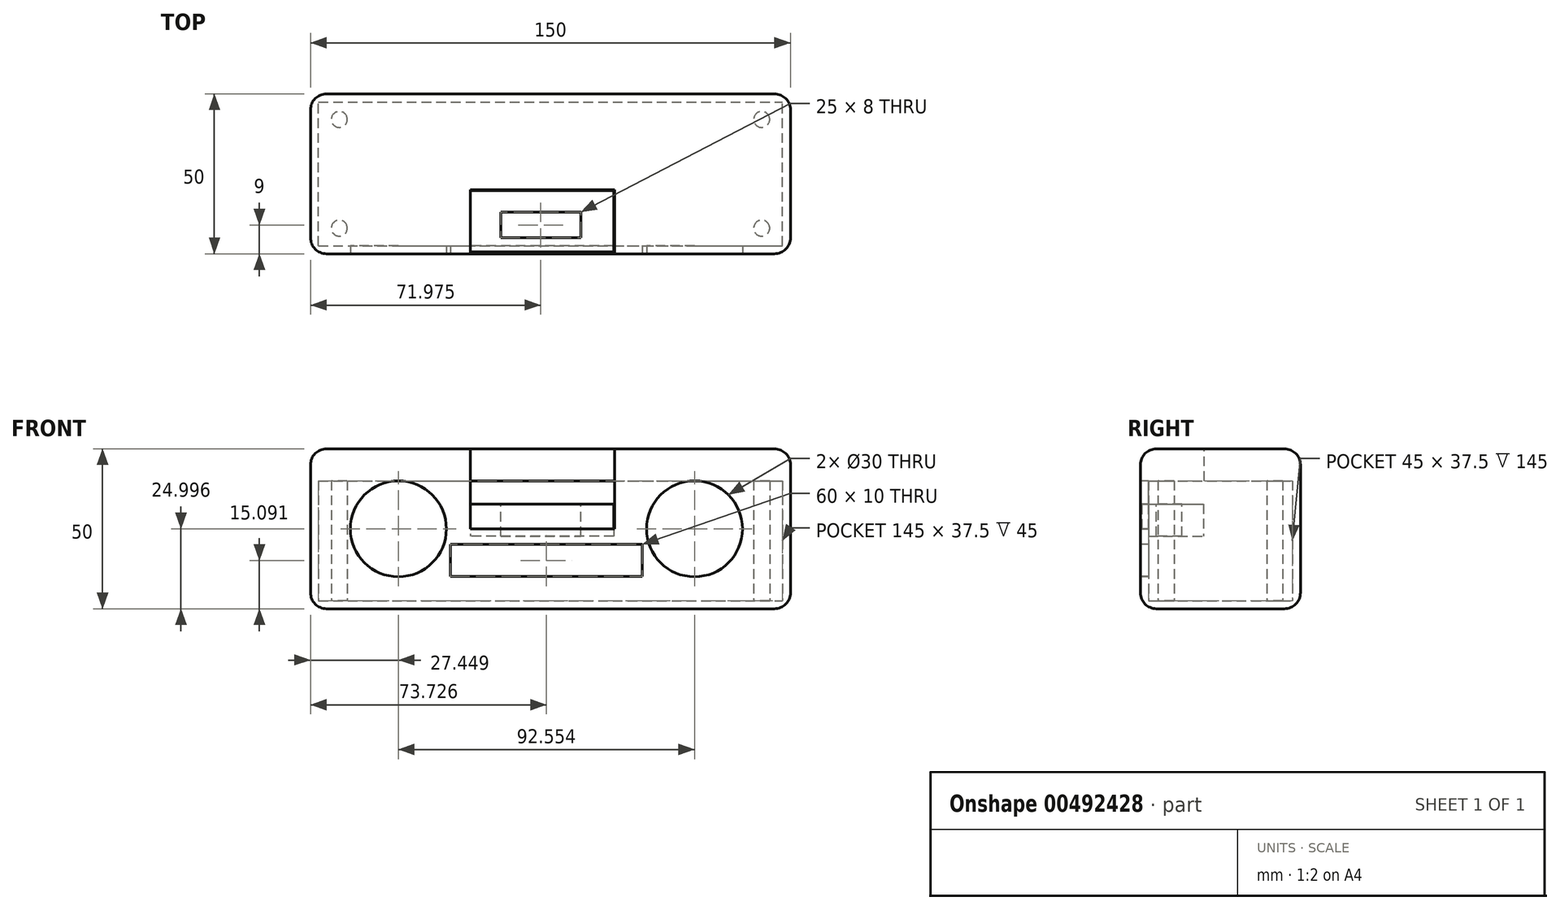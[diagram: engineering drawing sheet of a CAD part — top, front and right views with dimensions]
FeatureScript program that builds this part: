
annotation { "Feature Type Name" : "Feature", "Feature Type Description" : "" }
export const myFeature = defineFeature(function(context is Context, id is Id, definition is map)
    precondition{}
    {
        {
            var Q0;
            Q0=qCreatedBy(makeId("Front.planeOp"),FACE);
            var sketch = newSketch(context, id + "F0", { "sketchPlane" : qUnion([Q0])});
            skLineSegment(sketch, "E0.bottom", {"start": v(-76.49, 17.3) * mm, "end": v(73.51, 17.3) * mm});
            skLineSegment(sketch, "E0.top", {"start": v(-76.49, -22.7) * mm, "end": v(73.51, -22.7) * mm});
            skLineSegment(sketch, "E0.left", {"start": v(-76.49, 17.3) * mm, "end": v(-76.49, -22.7) * mm});
            skLineSegment(sketch, "E0.right", {"start": v(73.51, 17.3) * mm, "end": v(73.51, -22.7) * mm});
            skSolve(sketch);
        }
        {
            var Q0;
            Q0=makeQuery(id+"F0.imprint","IMPRINT",FACE,{"disambiguationData":[TD([[makeQuery(id+"F0.imprint","IMPRINT",EDGE,{"derivedFrom":sQuery(id+"F0.wireOp",EDGE,"E0.bottom")}),-1.0]])]});
            extrude(context, id + "F1", {"entities" : qUnion([Q0]), "depth" : 50 * mm});
        }
        {
            var Q0;
            Q0=makeQuery(id+"F1.opExtrude","SWEPT_FACE",FACE,{"disambiguationData":[OSD([sQuery(id+"F0.wireOp",EDGE,"E0.bottom")])]});
            shell(context, id + "F2", {"entities" : qUnion([Q0]), "thickness" : 2.5 * mm});
        }
        {
            var Q0;
            Q0=makeQuery(id+"F2.opShell","OFFSET_FACE",FACE,{"disambiguationData":[OSD([sQuery(id+"F0.wireOp",EDGE,"E0.top")])]});
            var sketch = newSketch(context, id + "F3", { "sketchPlane" : qUnion([Q0])});
            skCircle(sketch, "E1", {"center": v(-67.49, -8) * mm, "radius": 2.5 * mm});
            skSolve(sketch);
        }
        {
            var Q0;
            Q0=makeQuery(id+"F3.imprint","IMPRINT",FACE,{"disambiguationData":[TD([[makeQuery(id+"F3.imprint","IMPRINT",EDGE,{"derivedFrom":sQuery(id+"F3.wireOp",EDGE,"E1")}),-1.0]])]});
            var sketch = newSketch(context, id + "F4", { "sketchPlane" : qUnion([Q0])});
            skCircle(sketch, "E2", {"center": v(64.51, -8) * mm, "radius": 2.5 * mm});
            skSolve(sketch);
        }
        {
            var Q0;
            Q0=makeQuery(id+"F3.imprint","IMPRINT",FACE,{"disambiguationData":[TD([[makeQuery(id+"F3.imprint","IMPRINT",EDGE,{"derivedFrom":sQuery(id+"F3.wireOp",EDGE,"E1")}),-1.0]])]});
            var sketch = newSketch(context, id + "F5", { "sketchPlane" : qUnion([Q0])});
            skCircle(sketch, "E3", {"center": v(64.51, -42) * mm, "radius": 2.5 * mm});
            skSolve(sketch);
        }
        {
            var Q0;
            Q0=makeQuery(id+"F3.imprint","IMPRINT",FACE,{"disambiguationData":[TD([[makeQuery(id+"F3.imprint","IMPRINT",EDGE,{"derivedFrom":sQuery(id+"F3.wireOp",EDGE,"E1")}),-1.0]])]});
            var sketch = newSketch(context, id + "F6", { "sketchPlane" : qUnion([Q0])});
            skCircle(sketch, "E4", {"center": v(-67.49, -42) * mm, "radius": 2.5 * mm});
            skSolve(sketch);
        }
        {
            var Q0;
            Q0 = qSketchRegion(id + "F5", true);
            extrude(context, id + "F7", {"entities" : qUnion([Q0]), "operationType" : NewBodyOperationType.ADD, "depth" : 40 * mm});
        }
        {
            var Q0;
            Q0 = qSketchRegion(id + "F6", true);
            extrude(context, id + "F8", {"entities" : qUnion([Q0]), "operationType" : NewBodyOperationType.ADD, "depth" : 40 * mm});
        }
        {
            var Q0;
            Q0 = qSketchRegion(id + "F4", true);
            extrude(context, id + "F9", {"entities" : qUnion([Q0]), "operationType" : NewBodyOperationType.ADD, "depth" : 40 * mm});
        }
        {
            var Q0;
            Q0 = qSketchRegion(id + "F3", true);
            extrude(context, id + "F10", {"entities" : qUnion([Q0]), "operationType" : NewBodyOperationType.ADD, "depth" : 40 * mm});
        }
        {
            var Q0;
            Q0=makeQuery(id+"F1.opExtrude","SWEPT_FACE",FACE,{"disambiguationData":[OSD([sQuery(id+"F0.wireOp",EDGE,"E0.bottom")])]});
            var sketch = newSketch(context, id + "F11", { "sketchPlane" : qUnion([Q0])});
            skLineSegment(sketch, "E5.bottom", {"start": v(-76.49, 0) * mm, "end": v(73.51, 0) * mm});
            skLineSegment(sketch, "E5.top", {"start": v(-76.49, -50) * mm, "end": v(73.51, -50) * mm});
            skLineSegment(sketch, "E5.left", {"start": v(-76.49, 0) * mm, "end": v(-76.49, -50) * mm});
            skLineSegment(sketch, "E5.right", {"start": v(73.51, 0) * mm, "end": v(73.51, -50) * mm});
            skSolve(sketch);
        }
        {
            var Q0;
            Q0 = qSketchRegion(id + "F11", true);
            extrude(context, id + "F12", {"entities" : qUnion([Q0]), "operationType" : NewBodyOperationType.ADD, "depth" : 10 * mm});
        }
        {
            var Q0;
            Q0=makeQuery(id+"F12.opExtrude","CAP_FACE",FACE,{"disambiguationData":[OSD([sQuery(id+"F11.wireOp",EDGE,"E5.bottom"),sQuery(id+"F11.wireOp",EDGE,"E5.top"),sQuery(id+"F11.wireOp",EDGE,"E5.left"),sQuery(id+"F11.wireOp",EDGE,"E5.right")])],"isStart":false});
            var sketch = newSketch(context, id + "F13", { "sketchPlane" : qUnion([Q0])});
            skLineSegment(sketch, "E6.bottom", {"start": v(-26.49, -50) * mm, "end": v(18.51, -50) * mm});
            skLineSegment(sketch, "E6.top", {"start": v(-26.49, -30) * mm, "end": v(18.51, -30) * mm});
            skLineSegment(sketch, "E6.left", {"start": v(-26.49, -50) * mm, "end": v(-26.49, -30) * mm});
            skLineSegment(sketch, "E6.right", {"start": v(18.51, -50) * mm, "end": v(18.51, -30) * mm});
            skSolve(sketch);
        }
        {
            var Q0;
            Q0=makeQuery(id+"F13.imprint","IMPRINT",FACE,{"disambiguationData":[TD([[makeQuery(id+"F13.imprint","IMPRINT",EDGE,{"derivedFrom":sQuery(id+"F13.wireOp",EDGE,"E6.bottom")}),1.0]])]});
            extrude(context, id + "F14", {"entities" : qUnion([Q0]), "operationType" : NewBodyOperationType.REMOVE, "oppositeDirection" : true, "depth" : 25 * mm});
        }
        {
            var Q0;
            Q0=qCreatedBy(makeId("Top.planeOp"),FACE);
            var sketch = newSketch(context, id + "F15", { "sketchPlane" : qUnion([Q0])});
            skLineSegment(sketch, "E7.bottom", {"start": v(-26.54, -49.46) * mm, "end": v(18.27, -49.46) * mm});
            skLineSegment(sketch, "E7.top", {"start": v(-26.54, -30.26) * mm, "end": v(18.27, -30.26) * mm});
            skLineSegment(sketch, "E7.left", {"start": v(-26.54, -49.46) * mm, "end": v(-26.54, -30.26) * mm});
            skLineSegment(sketch, "E7.right", {"start": v(18.27, -49.46) * mm, "end": v(18.27, -30.26) * mm});
            skSolve(sketch);
        }
        {
            var Q0;
            Q0 = qSketchRegion(id + "F15", true);
            extrude(context, id + "F16", {"entities" : qUnion([Q0]), "operationType" : NewBodyOperationType.ADD, "depth" : 10 * mm});
        }
        {
            var Q0;
            Q0=makeQuery(id+"F16.opExtrude","CAP_FACE",FACE,{"disambiguationData":[OSD([sQuery(id+"F15.wireOp",EDGE,"E7.bottom"),sQuery(id+"F15.wireOp",EDGE,"E7.top"),sQuery(id+"F15.wireOp",EDGE,"E7.left"),sQuery(id+"F15.wireOp",EDGE,"E7.right")])],"isStart":false});
            var sketch = newSketch(context, id + "F17", { "sketchPlane" : qUnion([Q0])});
            skLineSegment(sketch, "E8.bottom", {"start": v(-17.02, -37) * mm, "end": v(7.98, -37) * mm});
            skLineSegment(sketch, "E8.top", {"start": v(-17.02, -45) * mm, "end": v(7.98, -45) * mm});
            skLineSegment(sketch, "E8.left", {"start": v(-17.02, -37) * mm, "end": v(-17.02, -45) * mm});
            skLineSegment(sketch, "E8.right", {"start": v(7.98, -37) * mm, "end": v(7.98, -45) * mm});
            skSolve(sketch);
        }
        {
            var Q0;
            Q0=makeQuery(id+"F17.imprint","IMPRINT",FACE,{"disambiguationData":[TD([[makeQuery(id+"F17.imprint","IMPRINT",EDGE,{"derivedFrom":sQuery(id+"F17.wireOp",EDGE,"E8.bottom")}),-1.0]])]});
            extrude(context, id + "F18", {"entities" : qUnion([Q0]), "operationType" : NewBodyOperationType.REMOVE, "oppositeDirection" : true, "depth" : 25 * mm});
        }
        {
            var Q0;
            Q0=makeQuery(id+"F12.boolean.opBoolean","MERGE",FACE,{"derivedFrom":[makeQuery(id+"F1.opExtrude","CAP_FACE",FACE,{"disambiguationData":[OSD([sQuery(id+"F0.wireOp",EDGE,"E0.bottom"),sQuery(id+"F0.wireOp",EDGE,"E0.top"),sQuery(id+"F0.wireOp",EDGE,"E0.left"),sQuery(id+"F0.wireOp",EDGE,"E0.right")])],"isStart":false}),makeQuery(id+"F12.opExtrude","SWEPT_FACE",FACE,{"disambiguationData":[OSD([sQuery(id+"F11.wireOp",EDGE,"E5.top")])]})]});
            var sketch = newSketch(context, id + "F19", { "sketchPlane" : qUnion([Q0])});
            skCircle(sketch, "E9", {"center": v(-49.04, 2.3) * mm, "radius": 15 * mm});
            skCircle(sketch, "E10", {"center": v(43.51, 2.3) * mm, "radius": 15 * mm});
            skSolve(sketch);
        }
        {
            var Q0;
            Q0=makeQuery(id+"F19.imprint","IMPRINT",FACE,{"disambiguationData":[TD([[makeQuery(id+"F19.imprint","IMPRINT",EDGE,{"derivedFrom":sQuery(id+"F19.wireOp",EDGE,"E9")}),1.0]])]});
            var Q1;
            Q1=makeQuery(id+"F19.imprint","IMPRINT",FACE,{"disambiguationData":[TD([[makeQuery(id+"F19.imprint","IMPRINT",EDGE,{"derivedFrom":sQuery(id+"F19.wireOp",EDGE,"E10")}),1.0]])]});
            extrude(context, id + "F20", {"entities" : qUnion([Q0, Q1]), "operationType" : NewBodyOperationType.REMOVE, "oppositeDirection" : true, "depth" : 5 * mm});
        }
        {
            var Q0;
            Q0=makeQuery(id+"F1.opExtrude","CAP_EDGE",EDGE,{"disambiguationData":[OSD([sQuery(id+"F0.wireOp",EDGE,"E0.top")])],"isStart":false});
            var Q1;
            Q1=makeQuery(id+"F1.opExtrude","SWEPT_EDGE",EDGE,{"disambiguationData":[OSD([sQuery(id+"F0.wireOp",EDGE,"E0.top"),sQuery(id+"F0.wireOp",EDGE,"E0.right")])]});
            var Q2;
            Q2=makeQuery(id+"F1.opExtrude","SWEPT_EDGE",EDGE,{"disambiguationData":[OSD([sQuery(id+"F0.wireOp",EDGE,"E0.top"),sQuery(id+"F0.wireOp",EDGE,"E0.left")])]});
            var Q3;
            Q3=makeQuery(id+"F1.opExtrude","CAP_EDGE",EDGE,{"disambiguationData":[OSD([sQuery(id+"F0.wireOp",EDGE,"E0.top")])],"isStart":true});
            var Q4;
            Q4=makeQuery(id+"F12.opExtrude","CAP_EDGE",EDGE,{"disambiguationData":[OSD([sQuery(id+"F11.wireOp",EDGE,"E5.bottom")])],"isStart":false});
            var Q5;
            {var subQ0=sQuery(id+"F11.wireOp",EDGE,"E5.top");var subQ1=sQuery(id+"F0.wireOp",EDGE,"E0.left");Q5=makeQuery(id+"F14.boolean.opBoolean","SPLIT",EDGE,{"disambiguationData":[TD([makeQuery(id+"F1.opExtrude","SWEPT_FACE",FACE,{"disambiguationData":[OSD([subQ1])]})])],"derivedFrom":makeQuery(id+"F12.opExtrude","CAP_EDGE",EDGE,{"disambiguationData":[OSD([subQ0])],"isStart":false})});}
            fillet(context, id + "F21", {"entities" : qUnion([Q0, Q1, Q2, Q3, Q4, Q5]), "radius" : 5 * mm, "tangentPropagation" : true, "allowEdgeOverflow" : false});
        }
        {
            var Q0;
            Q0=makeQuery(id+"F12.opExtrude","CAP_EDGE",EDGE,{"disambiguationData":[OSD([sQuery(id+"F11.wireOp",EDGE,"E5.right")])],"isStart":false});
            var Q1;
            Q1=makeQuery(id+"F12.opExtrude","CAP_EDGE",EDGE,{"disambiguationData":[OSD([sQuery(id+"F11.wireOp",EDGE,"E5.left")])],"isStart":false});
            var Q2;
            Q2=makeQuery(id+"F12.boolean.opBoolean","MERGE",EDGE,{"derivedFrom":[makeQuery(id+"F1.opExtrude","CAP_EDGE",EDGE,{"disambiguationData":[OSD([sQuery(id+"F0.wireOp",EDGE,"E0.right")])],"isStart":false}),makeQuery(id+"F12.opExtrude","SWEPT_EDGE",EDGE,{"disambiguationData":[OSD([sQuery(id+"F11.wireOp",EDGE,"E5.top"),sQuery(id+"F11.wireOp",EDGE,"E5.right")])]})]});
            fillet(context, id + "F22", {"entities" : qUnion([Q0, Q1, Q2]), "radius" : 5 * mm, "tangentPropagation" : true, "allowEdgeOverflow" : false});
        }
        {
            var Q0;
            {var subQ0=sQuery(id+"F11.wireOp",EDGE,"E5.top");var subQ1=sQuery(id+"F0.wireOp",EDGE,"E0.right");Q0=makeQuery(id+"F14.boolean.opBoolean","SPLIT",EDGE,{"disambiguationData":[TD([makeQuery(id+"F1.opExtrude","SWEPT_FACE",FACE,{"disambiguationData":[OSD([subQ1])]})])],"derivedFrom":makeQuery(id+"F12.opExtrude","CAP_EDGE",EDGE,{"disambiguationData":[OSD([subQ0])],"isStart":false})});}
            fillet(context, id + "F23", {"entities" : qUnion([Q0]), "radius" : 5 * mm, "tangentPropagation" : true, "allowEdgeOverflow" : false});
        }
        {
            var Q0;
            Q0=makeQuery(id+"F19.imprint","IMPRINT",FACE,{"disambiguationData":[TD([[makeQuery(id+"F19.imprint","IMPRINT",EDGE,{"derivedFrom":sQuery(id+"F19.wireOp",EDGE,"E9")}),-1.0]])]});
            var sketch = newSketch(context, id + "F24", { "sketchPlane" : qUnion([Q0])});
            skLineSegment(sketch, "E11.bottom", {"start": v(-32.76, -2.6) * mm, "end": v(27.24, -2.6) * mm});
            skLineSegment(sketch, "E11.top", {"start": v(-32.76, -12.6) * mm, "end": v(27.24, -12.6) * mm});
            skLineSegment(sketch, "E11.left", {"start": v(-32.76, -2.6) * mm, "end": v(-32.76, -12.6) * mm});
            skLineSegment(sketch, "E11.right", {"start": v(27.24, -2.6) * mm, "end": v(27.24, -12.6) * mm});
            skSolve(sketch);
        }
        {
            var Q0;
            Q0=makeQuery(id+"F24.imprint","IMPRINT",FACE,{"disambiguationData":[TD([[makeQuery(id+"F24.imprint","IMPRINT",EDGE,{"derivedFrom":sQuery(id+"F24.wireOp",EDGE,"E11.bottom")}),-1.0]])]});
            extrude(context, id + "F25", {"entities" : qUnion([Q0]), "operationType" : NewBodyOperationType.REMOVE, "oppositeDirection" : true, "depth" : 25 * mm});
        }
    });
